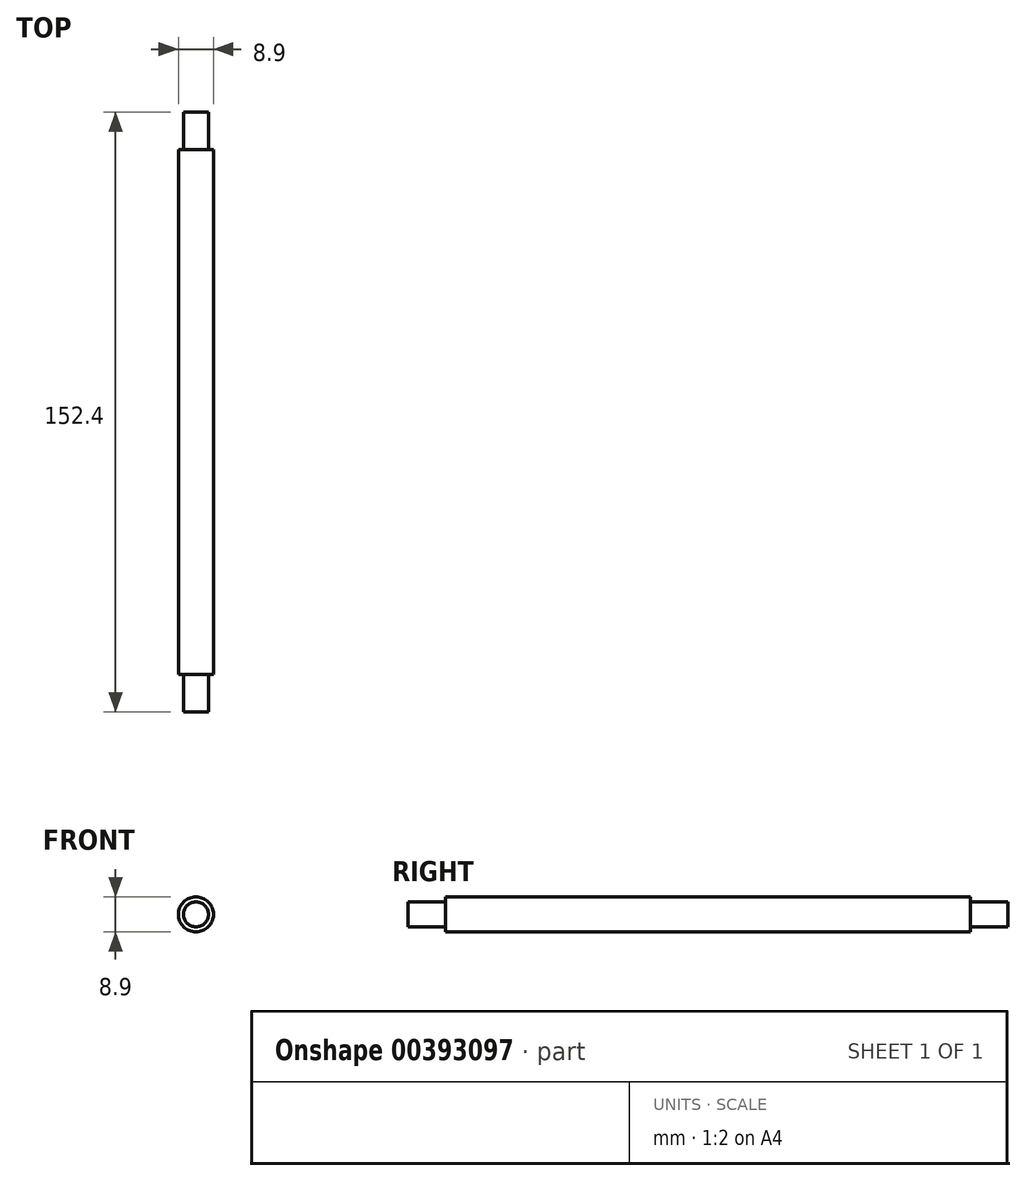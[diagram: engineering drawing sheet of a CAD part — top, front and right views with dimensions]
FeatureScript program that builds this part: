
annotation { "Feature Type Name" : "Feature", "Feature Type Description" : "" }
export const myFeature = defineFeature(function(context is Context, id is Id, definition is map)
    precondition{}
    {
        {
            var Q0;
            Q0=qCreatedBy(makeId("Top.planeOp"),FACE);
            var sketch = newSketch(context, id + "F0", { "sketchPlane" : qUnion([Q0])});
            skLineSegment(sketch, "E0.bottom", {"start": v(3.17, -66.68) * mm, "end": v(4.45, -66.68) * mm});
            skLineSegment(sketch, "E0.top", {"start": v(3.18, 66.68) * mm, "end": v(4.45, 66.68) * mm});
            skLineSegment(sketch, "E0.right", {"start": v(4.45, -66.68) * mm, "end": v(4.44, 66.68) * mm});
            skLineSegment(sketch, "E1", {"start": v(3.17, -66.68) * mm, "end": v(3.17, -76.2) * mm});
            skLineSegment(sketch, "E2", {"start": v(3.17, -76.2) * mm, "end": v(0, -76.2) * mm});
            skPoint(sketch, "E0.left.start.orphan", {"position": v(0, -66.68) * mm});
            skLineSegment(sketch, "E3", {"start": v(3.18, 66.68) * mm, "end": v(3.17, 76.2) * mm});
            skLineSegment(sketch, "E4", {"start": v(3.17, 76.2) * mm, "end": v(0, 76.2) * mm});
            skLineSegment(sketch, "E5", {"start": v(0, 76.2) * mm, "end": v(0, -76.2) * mm});
            skSolve(sketch);
        }
        {
            var Q0;
            Q0=makeQuery(id+"F0.imprint","IMPRINT",FACE,{"disambiguationData":[TD([[makeQuery(id+"F0.imprint","IMPRINT",EDGE,{"derivedFrom":sQuery(id+"F0.wireOp",EDGE,"E0.bottom")}),1.0]])]});
            var Q1;
            Q1=sQuery(id+"F0.wireOp",EDGE,"E5");
            revolve(context, id + "F1", {"entities" : qUnion([Q0]), "axis" : qUnion([Q1]), "revolveType" : RevolveType.FULL});
        }
    });
